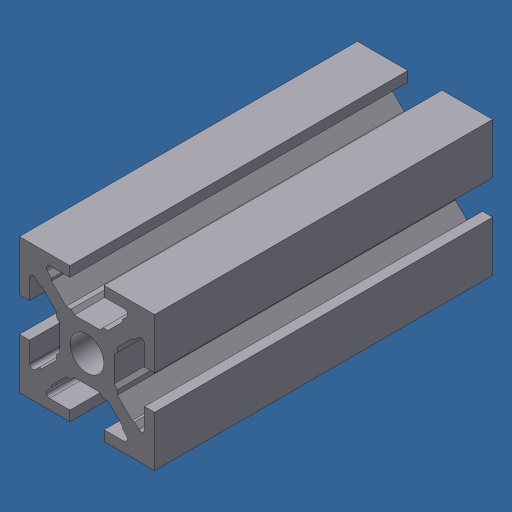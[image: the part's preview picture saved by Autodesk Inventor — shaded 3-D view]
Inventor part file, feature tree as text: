
AUTODESK INVENTOR PART (.ipt)
format: ipt  version: 2024.3 (Build 283343000, 343)  size: 254,976 bytes
history: native  units: mm (DEFAULTED — no unit token found)
features: extrude x2, sketch x2, other x1
ambient origin geometry x8: Origin, YZ Plane, XZ Plane, XY Plane, X Axis, Y Axis, Z Axis, Center Point
bodies: Body1 (feature_tree)
feature tree (5):
  other  "Finish - None"
  extrude  "MK, 40X40"  Depth=14.95mm
  extrude  "Extrusion2"  Depth=3.0mm
  sketch  "Sketch1"  dims[d0=10.0mm d3=14.95mm]
  sketch  "Sketch2"  dims[d4=14.95mm d5=3.0mm d7=2.0mm d8=4.0mm d9=4.0mm d10=8.949804mm d11=8.949804mm d12=45.0deg d16=8.0mm d18=2.5mm d19=20.0mm d21=1.0mm d22=100.0mm d23=0.0mm d24=0.5mm d25=0.5mm d26=1.0mm d28=4.0mm d29=0.5mm d30=10.5mm d31=10.5mm d32=100.0mm d33=0.0mm d34=8.0mm]
